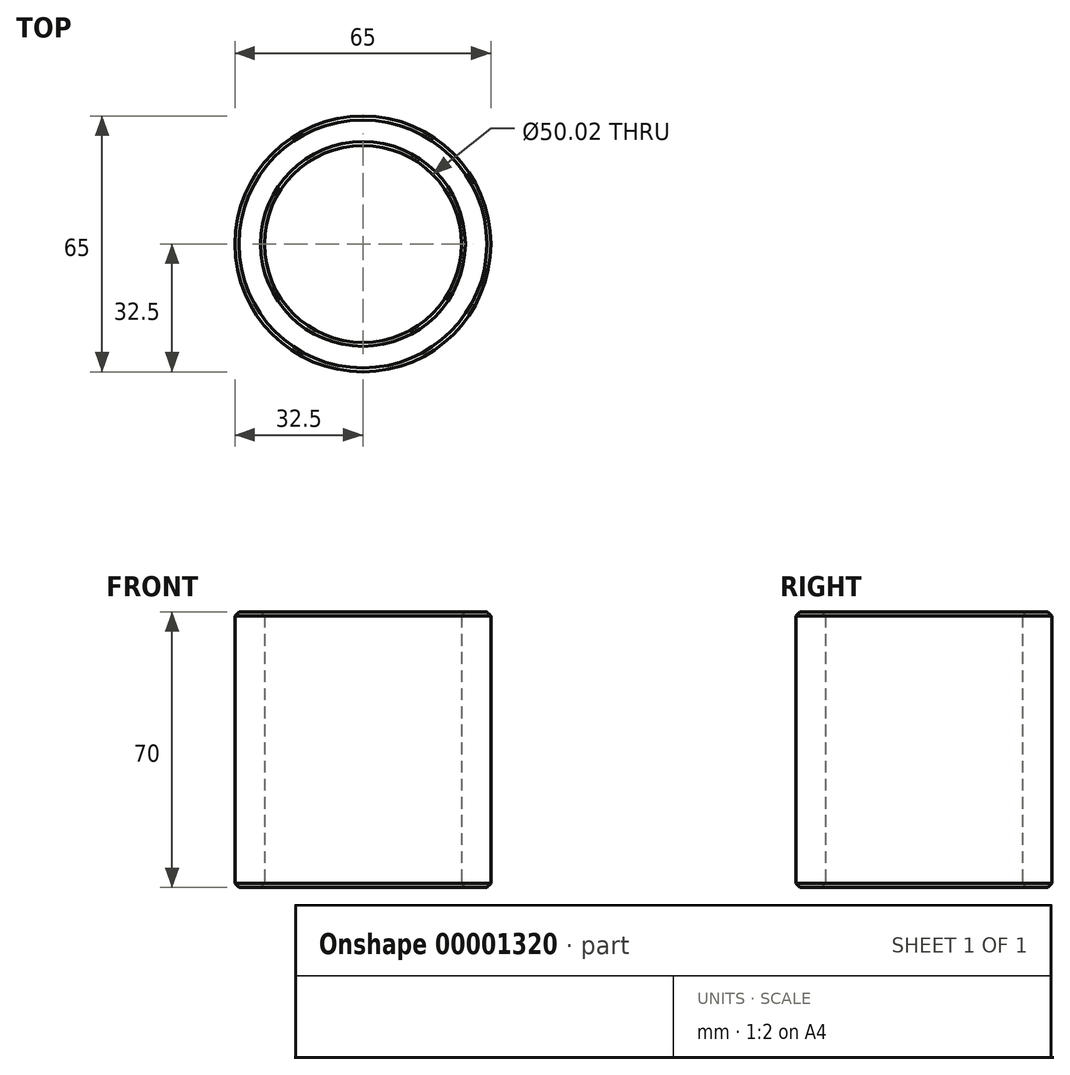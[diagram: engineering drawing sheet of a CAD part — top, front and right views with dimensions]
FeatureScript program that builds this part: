
annotation { "Feature Type Name" : "Feature", "Feature Type Description" : "" }
export const myFeature = defineFeature(function(context is Context, id is Id, definition is map)
    precondition{}
    {
        {
            var Q0;
            Q0=qCreatedBy(makeId("Top.planeOp"),FACE);
            var sketch = newSketch(context, id + "F0", { "sketchPlane" : qUnion([Q0])});
            skCircle(sketch, "E0", {"center": v(0, 0) * mm, "radius": 25.01 * mm});
            skCircle(sketch, "E1", {"center": v(0, 0) * mm, "radius": 32.5 * mm});
            skSolve(sketch);
        }
        {
            var Q0;
            Q0=makeQuery(id+"F0.imprint","IMPRINT",FACE,{"disambiguationData":[TD([[makeQuery(id+"F0.imprint","IMPRINT",EDGE,{"derivedFrom":sQuery(id+"F0.wireOp",EDGE,"E0")}),-1.0]])]});
            extrude(context, id + "F1", {"entities" : qUnion([Q0]), "depth" : 70 * mm});
        }
        {
            var Q0;
            Q0=makeQuery(id+"F1.opExtrude","CAP_FACE",FACE,{"disambiguationData":[OSD([sQuery(id+"F0.wireOp",EDGE,"E0"),sQuery(id+"F0.wireOp",EDGE,"E1")])],"isStart":false});
            chamfer(context, id + "F2", {"entities" : qUnion([Q0]), "width" : 1 * mm, "tangentPropagation" : true});
        }
        {
            var Q0;
            Q0=makeQuery(id+"F1.opExtrude","CAP_FACE",FACE,{"disambiguationData":[OSD([sQuery(id+"F0.wireOp",EDGE,"E0"),sQuery(id+"F0.wireOp",EDGE,"E1")])],"isStart":true});
            chamfer(context, id + "F3", {"entities" : qUnion([Q0]), "width" : 1 * mm, "tangentPropagation" : true});
        }
    });
